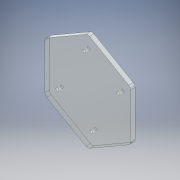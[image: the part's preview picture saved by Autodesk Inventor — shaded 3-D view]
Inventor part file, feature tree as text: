
AUTODESK INVENTOR PART (.ipt)
format: ipt  version: 2018 (Build 220112000, 112)  size: 151,040 bytes
history: native  units: mm
features: sketch x1, extrude x1, fillet x1
ambient origin geometry x8: Origin, YZ Plane, XZ Plane, XY Plane, X Axis, Y Axis, Z Axis, Center Point
bodies: Body1 (feature_tree)
feature tree (3):
  sketch  "Sketch1"  dims[d0=54.864mm d1=0.0mm d3=39.0mm d4=4.5mm d5=4.5mm d6=4.5mm d7=4.5mm d9=4.5mm d11=4.5mm d15=4.5mm d21=5.0mm d22=0.0mm d28=4.0mm]
  extrude  "Extrusion2"  Depth=5.0mm TaperAngle=0.0deg
  fillet  "Fillet1"  Radius=4.0mm
